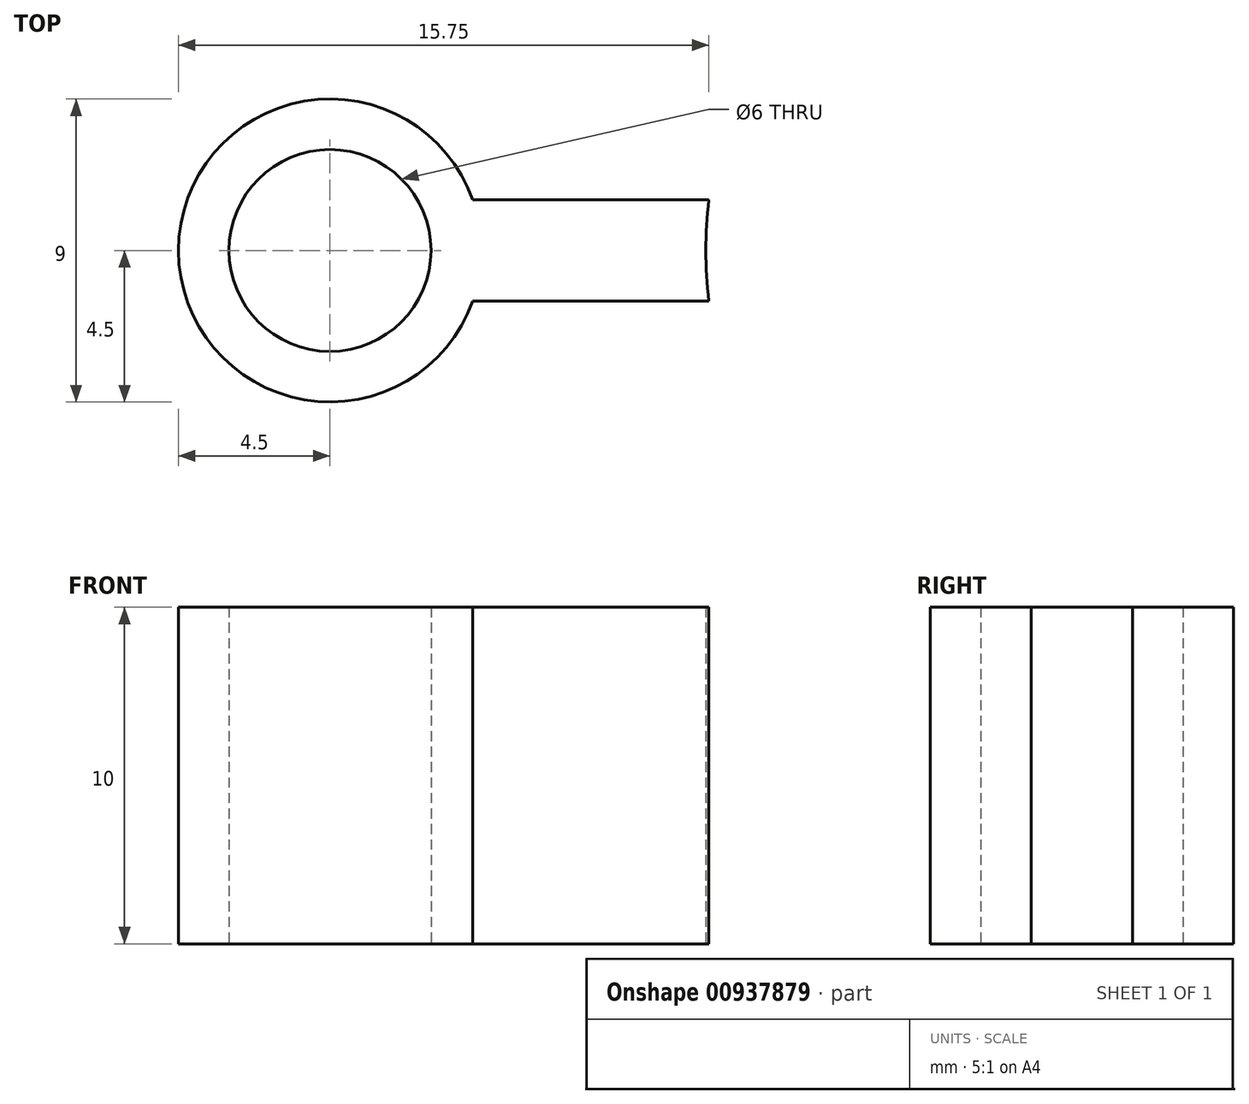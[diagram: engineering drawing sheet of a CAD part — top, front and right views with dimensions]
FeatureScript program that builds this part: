
annotation { "Feature Type Name" : "Feature", "Feature Type Description" : "" }
export const myFeature = defineFeature(function(context is Context, id is Id, definition is map)
    precondition{}
    {
        {
            var Q0;
            Q0=qCreatedBy(makeId("Top.planeOp"),FACE);
            var sketch = newSketch(context, id + "F0", { "sketchPlane" : qUnion([Q0])});
            skCircle(sketch, "E0", {"center": v(0, 0) * mm, "radius": 3 * mm});
            skCircle(sketch, "E1", {"center": v(0, 0) * mm, "radius": 4.5 * mm});
            skArc(sketch, "E2", {"start": v(11.25, 1.5) * mm, "mid": v(11.16, 0) * mm, "end": v(11.25, -1.5) * mm});
            skLineSegment(sketch, "E3", {"start": v(4.24, 1.5) * mm, "end": v(11.25, 1.5) * mm});
            skPoint(sketch, "E4.start.orphan", {"position": v(0, 4.5) * mm});
            skLineSegment(sketch, "E5", {"start": v(4.24, -1.5) * mm, "end": v(11.25, -1.5) * mm});
            skPoint(sketch, "E6.start.orphan", {"position": v(0, -4.5) * mm});
            skSolve(sketch);
        }
        {
            var Q0;
            Q0 = qSketchRegion(id + "F0", true);
            extrude(context, id + "F1", {"entities" : qUnion([Q0]), "depth" : 10 * mm, "offsetDistance" : 25 * mm});
        }
    });
